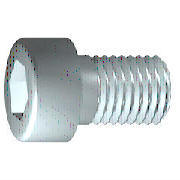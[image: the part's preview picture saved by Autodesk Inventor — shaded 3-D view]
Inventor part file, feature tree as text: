
AUTODESK INVENTOR PART (.ipt)
format: ipt  version: 2019 (Build 230136000, 136)  size: 202,240 bytes
history: native  units: mm (DEFAULTED — no unit token found)
features: sketch x2, extrude x1, plane x1, fillet x1
ambient origin geometry x7: Origin, YZ Plane, XY Plane, X Axis, Y Axis, Z Axis, Center Point
bodies: Solid1 (feature_tree), Body (feature_tree)
feature tree (5):
  extrude  "Slot"  Depth=5.0mm
  plane  "Work Plane1"
  fillet  "Fillet2"  Radius=5.0mm
  sketch  "Sketch1"  dims[d1=6.0mm d2=0.49086mm d3=5.0mm]
  sketch  "Sketch2"  dims[d4=2.5mm d5=60.0deg d6=5.0mm d7=5.0mm d8=4.618802mm d9=8.5mm d10=90.0deg d11=10.0mm d12=0.0mm d13=6.0mm d14=0.0mm d15=0.49076mm d16=0.49076mm d17=0.5mm d19=0.0mm d26=8.0mm d27=45.0deg d28=0.0mm d29=0.0mm d30=0.1mm]
